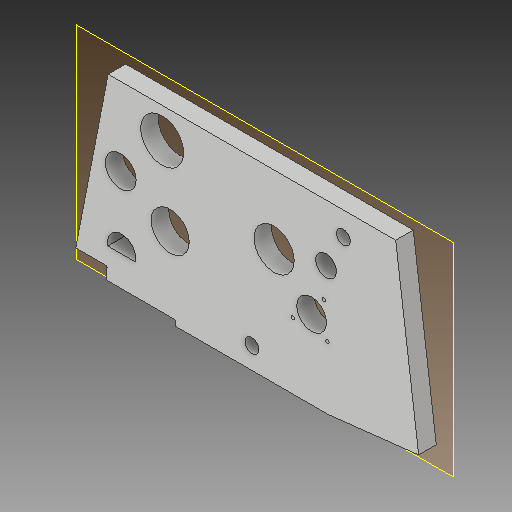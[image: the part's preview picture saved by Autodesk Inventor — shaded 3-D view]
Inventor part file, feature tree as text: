
AUTODESK INVENTOR PART (.ipt)
format: ipt  version: 2018 (Build 220112000, 112)  size: 150,528 bytes
history: native  units: in
note: dims shown in document units (in); Inventor stores cm internally (conversion verified against a paired STEP export)
features: other x5, extrude x2, sketch x2, plane x1, reference x1
ambient origin geometry x8: Origin, YZ Plane, XZ Plane, XY Plane, X Axis, Y Axis, Z Axis, Center Point
bodies: Solid1 (feature_tree)
feature tree (11):
  other  "Table"
  other  "Part11-01"
  other  "Part11-02"
  plane  "Work Plane1"
  extrude  "Extrusion1"  Depth=1.0in TaperAngle=0.0deg
  extrude  "Extrusion2"  [1 undecoded]
  sketch  "Sketch1"  dims[d0=1.0in d1=0.0in d3=1.0in d4=0.0in]
  reference  "Reference1"
  sketch  "Sketch2"
  other  "Lathe Model 2018.iam"
  other  "Gearbox:1"
note: 1 required parameter value undecoded (feature->parameter linkage not recoverable at this tier; creation-order binding heuristic only, values carry confidence <= 0.55)
